SOLIDWORKS PART (.sldprt)
format: sldprt  version: not decoded by parser v0  size: 536,064 bytes
history: native  units: mm
features: sketch x15, cut_extrude x8, extrude x5, plane x3, material x1 (+9 scaffold rows collapsed)
feature tree (41):
  scaffold x9  (default folders/planes/origin — collapsed)
  material  "Material <nicht festgelegt>"
  plane  "Ebene vorne"
  plane  "Ebene oben"
  plane  "Ebene rechts"
  sketch  "Skizze1"  dims[D1=0.8mm D2=1.5mm]
  extrude  "Aufsatz-Linear austragen1"  Depth=18mm
  sketch  "Skizze3"  dims[D1=0.0mm]
  extrude  "Aufsatz-Linear austragen2"  Depth=2mm
  sketch  "Skizze4"  dims[D1=0.0mm]
  cut_extrude  "Schnitt-Linear austragen1"  [1 undecoded]
  sketch  "Skizze5"  dims[D1=15.0mm D2=12.0mm D3=0.0mm]
  cut_extrude  "Schnitt-Linear austragen2"  [1 undecoded]
  sketch  "Skizze6"  dims[D1=10.0mm D2=10.0mm D3=~3.934802mm]
  sketch  "Skizze7"  dims[D1=3.0mm D2=0.12mm D3=0.12mm D4=0.12mm]
  extrude  "Aufsatz-Linear austragen3"  Depth=6.5mm
  sketch  "Skizze8"  dims[D2=4.6mm D3=4.6mm D4=4.6mm D5=4.6mm D6=13.9mm D7=13.9mm D8=~14.687061mm D1=3.0mm]
  extrude  "Aufsatz-Linear austragen4"  Depth=3mm
  sketch  "Skizze9"  dims[c1.D1=20.0mm c1.D2=10.0mm c2.D1=10.0mm c2.D2=10.0mm c2.D3=10.0mm c2.D4=10.0mm c2.D5=10.0mm c2.D6=10.0mm c2.D7=10.0mm c2.D8=10.0mm c2.D9=10.0mm c2.D10=10.0mm c2.D11=10.0mm c2.D12=10.0mm c2.D13=10.0mm c3.D3=1.0mm c3.D1=0.0mm c3.D14=1.0mm]
  extrude  "Aufsatz-Linear austragen7"  Depth=3mm
  sketch  "Skizze11"  dims[D2=5.0mm D3=10.0mm D4=10.0mm D1=0.0mm]
  cut_extrude  "Schnitt-Linear austragen3"  [1 undecoded]
  sketch  "Skizze12"  dims[D1=0.0mm]
  sketch  "Skizze13"  dims[D1=10.0mm D2=10.0mm]
  cut_extrude  "Schnitt-Linear austragen4"  [1 undecoded]
  sketch  "Skizze14"  dims[D1=10.0mm D2=10.0mm]
  cut_extrude  "Schnitt-Linear austragen5"  [1 undecoded]
  sketch  "Skizze15"  dims[D1=10.0mm D2=10.0mm]
  cut_extrude  "Schnitt-Linear austragen6"  [1 undecoded]
  sketch  "Skizze16"  dims[D1=10.0mm D2=10.0mm]
  cut_extrude  "Schnitt-Linear austragen7"  [1 undecoded]
  sketch  "Skizze17"  dims[D1=10.0mm D2=10.0mm]
  cut_extrude  "Schnitt-Linear austragen8"  [1 undecoded]
decode coverage: 20 of 28 modeling features carry decoded parameters
note: ~ marks probable driven/reference dimensions
note: 8 parameter values undecoded
summary: no parameter record found for 8 features
note: suppression state not decoded; provenance and decode notes live in map.json
